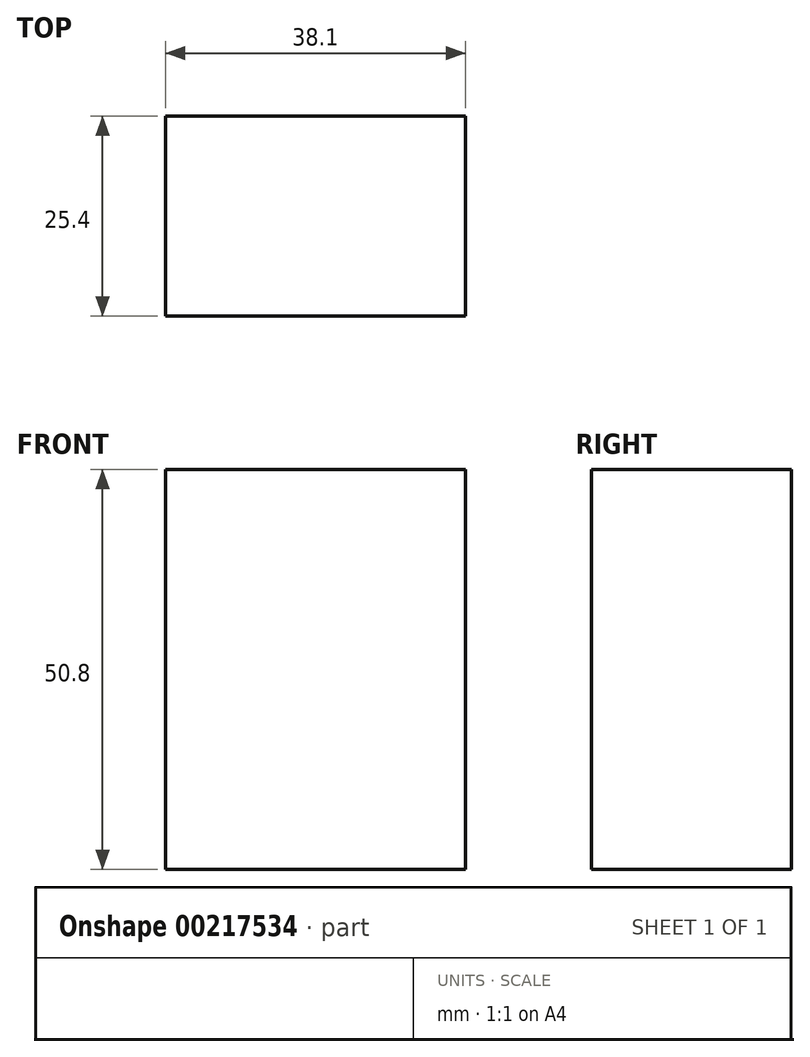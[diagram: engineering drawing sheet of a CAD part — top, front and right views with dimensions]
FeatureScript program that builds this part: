
annotation { "Feature Type Name" : "Feature", "Feature Type Description" : "" }
export const myFeature = defineFeature(function(context is Context, id is Id, definition is map)
    precondition{}
    {
        {
            var Q0;
            Q0=qCreatedBy(makeId("Front.planeOp"),FACE);
            var sketch = newSketch(context, id + "F0", { "sketchPlane" : qUnion([Q0])});
            skLineSegment(sketch, "E0.bottom", {"start": v(-19.05, 50.8) * mm, "end": v(19.05, 50.8) * mm});
            skLineSegment(sketch, "E0.top", {"start": v(-19.05, 0) * mm, "end": v(19.05, 0) * mm});
            skLineSegment(sketch, "E0.left", {"start": v(-19.05, 50.8) * mm, "end": v(-19.05, 0) * mm});
            skLineSegment(sketch, "E0.right", {"start": v(19.05, 50.8) * mm, "end": v(19.05, 0) * mm});
            skSolve(sketch);
        }
        {
            var Q0;
            Q0 = qSketchRegion(id + "F0", true);
            extrude(context, id + "F1", {"entities" : qUnion([Q0]), "depth" : 25.4 * mm});
        }
    });
